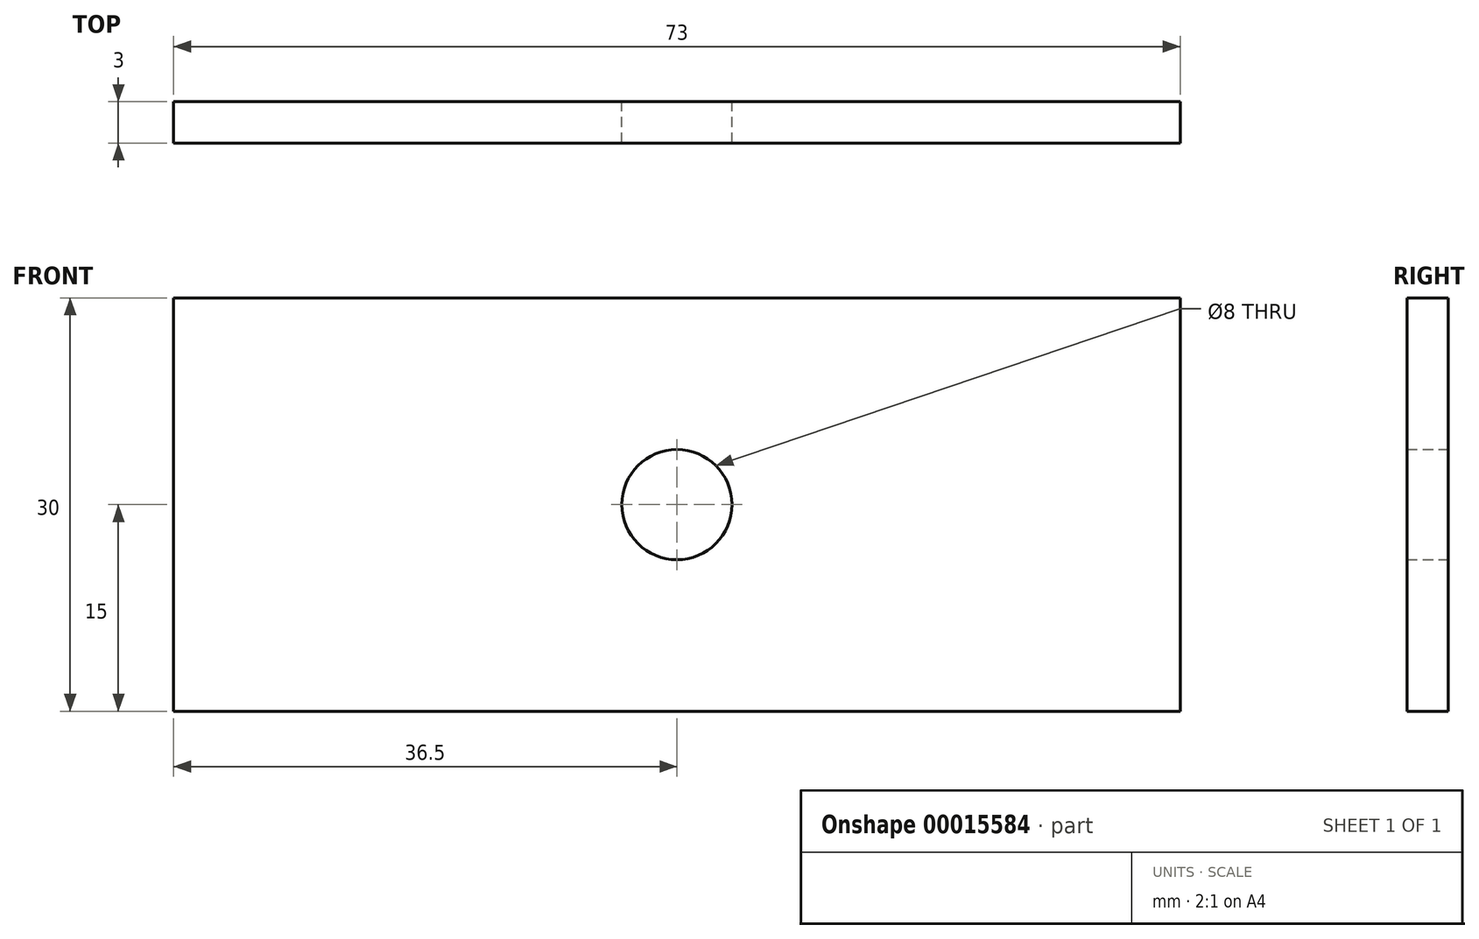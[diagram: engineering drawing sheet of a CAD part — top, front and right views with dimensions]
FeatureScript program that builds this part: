
annotation { "Feature Type Name" : "Feature", "Feature Type Description" : "" }
export const myFeature = defineFeature(function(context is Context, id is Id, definition is map)
    precondition{}
    {
        {
            var Q0;
            Q0=qCreatedBy(makeId("Front.planeOp"),FACE);
            var sketch = newSketch(context, id + "F0", { "sketchPlane" : qUnion([Q0])});
            skLineSegment(sketch, "E0.bottom", {"start": v(0, 0) * mm, "end": v(73, 0) * mm});
            skLineSegment(sketch, "E0.top", {"start": v(0, 30) * mm, "end": v(73, 30) * mm});
            skLineSegment(sketch, "E0.left", {"start": v(0, 0) * mm, "end": v(0, 30) * mm});
            skLineSegment(sketch, "E0.right", {"start": v(73, 0) * mm, "end": v(73, 30) * mm});
            skCircle(sketch, "E1", {"center": v(36.5, 15) * mm, "radius": 4 * mm});
            skSolve(sketch);
        }
        {
            var Q0;
            Q0=makeQuery(id+"F0.imprint","IMPRINT",FACE,{"disambiguationData":[TD([[makeQuery(id+"F0.imprint","IMPRINT",EDGE,{"derivedFrom":sQuery(id+"F0.wireOp",EDGE,"E0.bottom")}),1.0]])]});
            extrude(context, id + "F1", {"entities" : qUnion([Q0]), "depth" : 3 * mm});
        }
    });
